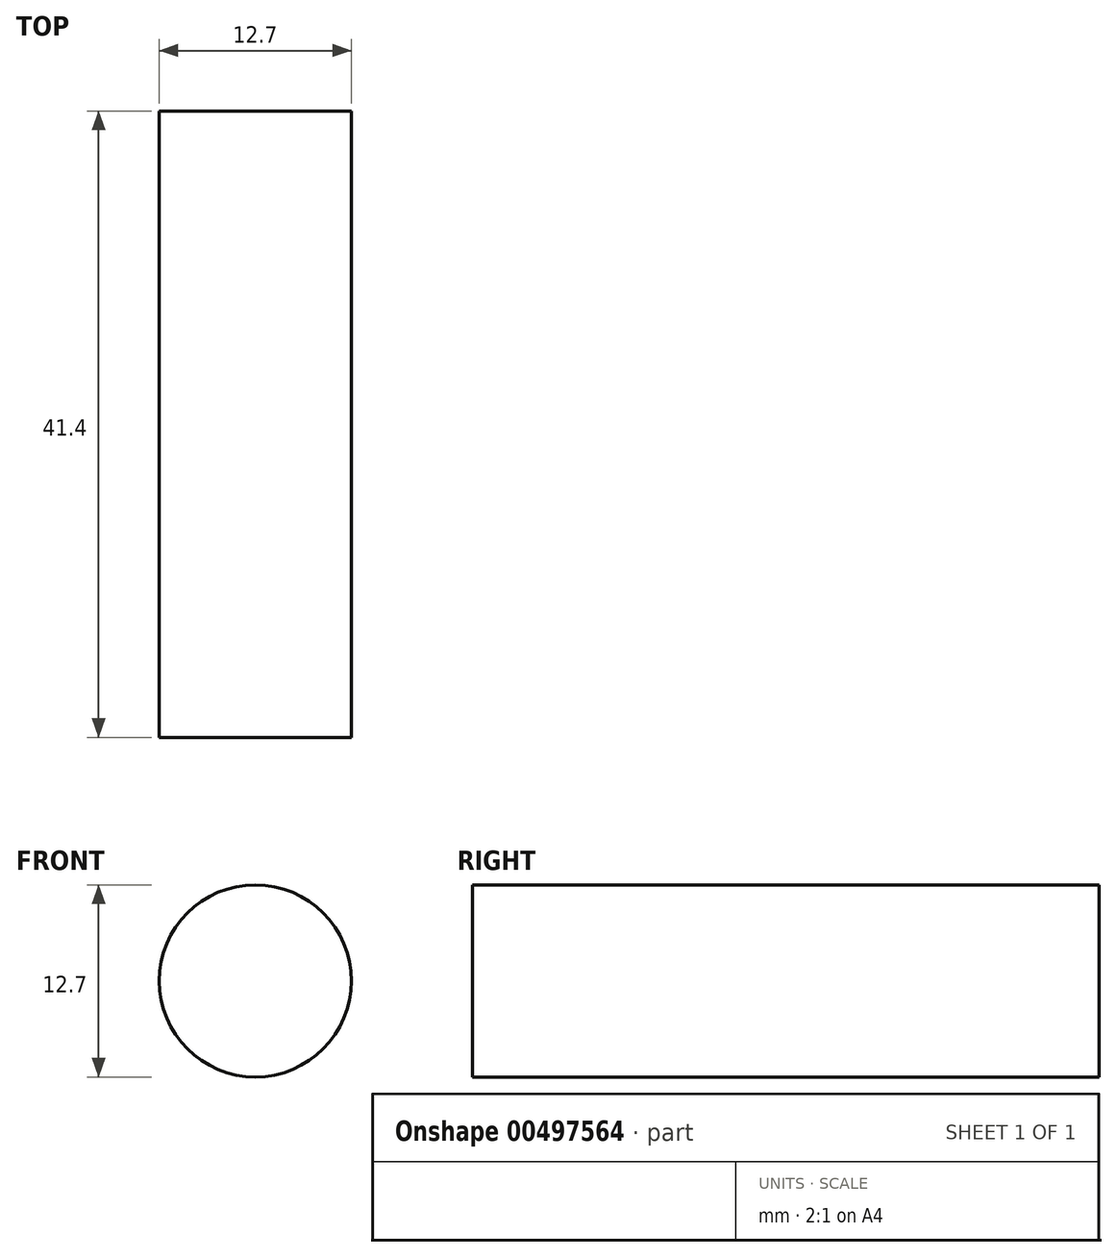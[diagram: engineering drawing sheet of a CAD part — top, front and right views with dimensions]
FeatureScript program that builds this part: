
annotation { "Feature Type Name" : "Feature", "Feature Type Description" : "" }
export const myFeature = defineFeature(function(context is Context, id is Id, definition is map)
    precondition{}
    {
        {
            var Q0;
            Q0=qCreatedBy(makeId("Front.planeOp"),FACE);
            var sketch = newSketch(context, id + "F0", { "sketchPlane" : qUnion([Q0])});
            skLineSegment(sketch, "E0", {"start": v(0, 0) * mm, "end": v(6.35, 0) * mm, "construction": true});
            skCircle(sketch, "E1", {"center": v(6.35, 0) * mm, "radius": 6.35 * mm});
            skSolve(sketch);
        }
        {
            var Q0;
            Q0=makeQuery(id+"F0.imprint","IMPRINT",FACE,{"disambiguationData":[TD([[makeQuery(id+"F0.imprint","IMPRINT",EDGE,{"derivedFrom":sQuery(id+"F0.wireOp",EDGE,"E1")}),1.0]])]});
            extrude(context, id + "F1", {"entities" : qUnion([Q0]), "depth" : 41.4 * mm});
        }
    });
